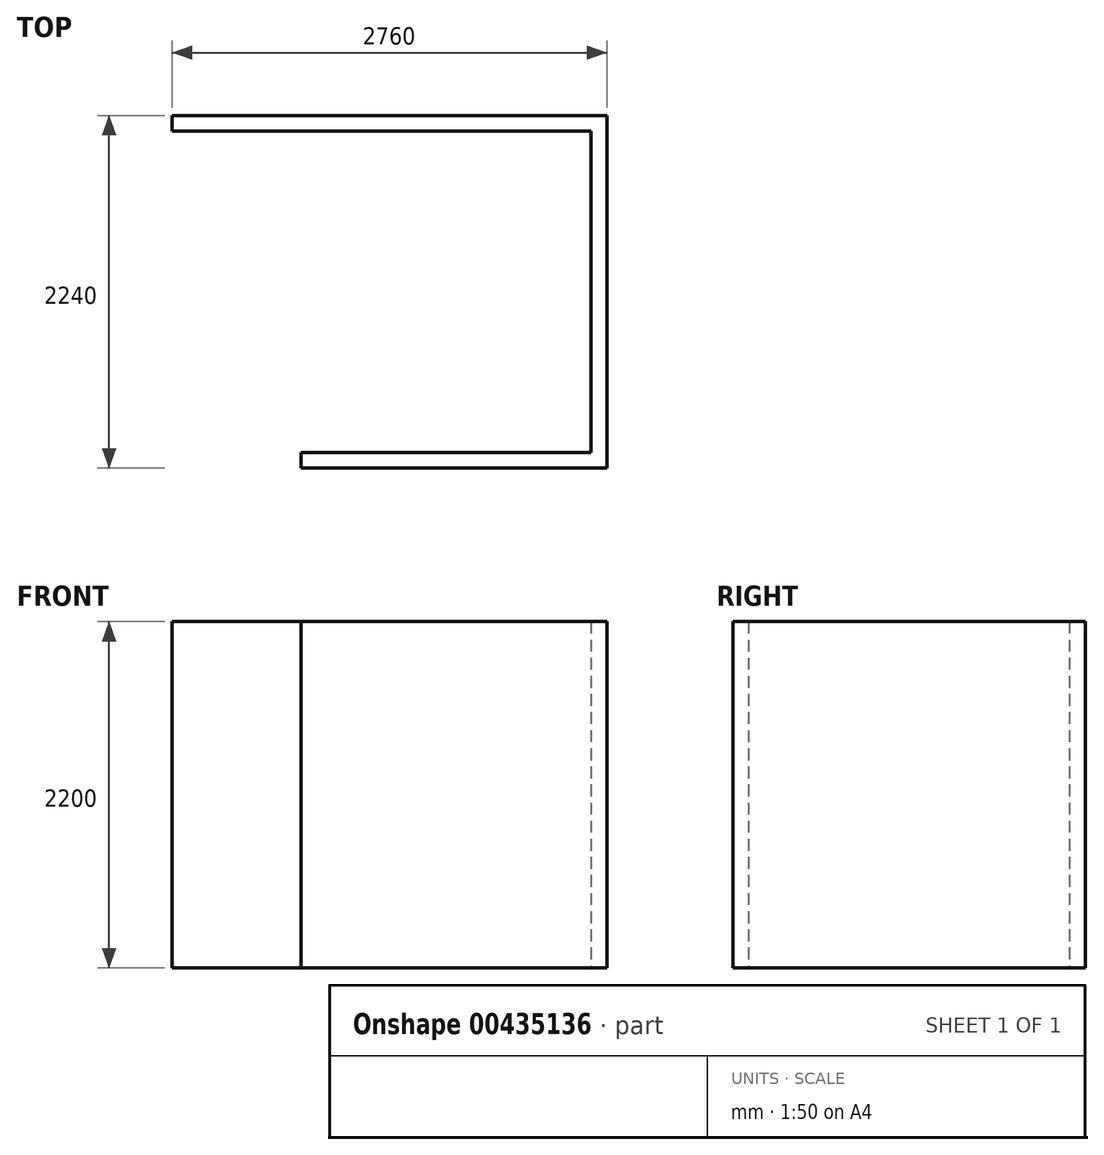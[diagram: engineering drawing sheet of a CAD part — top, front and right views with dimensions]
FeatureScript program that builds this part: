
annotation { "Feature Type Name" : "Feature", "Feature Type Description" : "" }
export const myFeature = defineFeature(function(context is Context, id is Id, definition is map)
    precondition{}
    {
        {
            var Q0;
            Q0=qCreatedBy(makeId("Top.planeOp"),FACE);
            var sketch = newSketch(context, id + "F0", { "sketchPlane" : qUnion([Q0])});
            skLineSegment(sketch, "E0", {"start": v(0, 100) * mm, "end": v(2760, 100) * mm});
            skLineSegment(sketch, "E1", {"start": v(2760, 100) * mm, "end": v(2760, -2140) * mm});
            skLineSegment(sketch, "E2", {"start": v(2760, -2140) * mm, "end": v(820, -2140) * mm});
            skLineSegment(sketch, "E3", {"start": v(820, -2140) * mm, "end": v(820, -2040) * mm});
            skLineSegment(sketch, "E4", {"start": v(820, -2040) * mm, "end": v(2660, -2040) * mm});
            skLineSegment(sketch, "E5", {"start": v(2660, -2040) * mm, "end": v(2660, 0) * mm});
            skLineSegment(sketch, "E6", {"start": v(2660, 0) * mm, "end": v(0, 0) * mm});
            skLineSegment(sketch, "E7", {"start": v(0, 0) * mm, "end": v(0, 100) * mm});
            skSolve(sketch);
        }
        {
            var Q0;
            Q0 = qSketchRegion(id + "F0", true);
            extrude(context, id + "F1", {"entities" : qUnion([Q0]), "depth" : 2200 * mm});
        }
    });
